FCSTD DOCUMENT  (FreeCAD 0.14R3702 (Git))
Label: big-gear-43_tooth-modified
License: CC-BY 3.0
LicenseURL: http://creativecommons.org/licenses/by/3.0/
objects: Part::Feature×1, Sketcher::SketchObject×1
note: 2 computed .brp shape members not serialized (recipe doc carries the construction recipe); baked Part::Feature solids carry a one-line shape summary decoded from their .brp

FEATURE [Part::Feature] Big_Gear_43_tooth_Less_Material001_solid  label="Big_Gear_43_tooth_Less_Material001 (Solid)"
  shape: large baked B-rep (63 MB .brp); summary skipped
FEATURE [Sketcher::SketchObject] Sketch
  ExternalGeometry = -> [Big_Gear_43_tooth_Less_Material001_solid]
  Placement = pos=(0,0,4) rot=(1,0,0;3.14159rad)
  Support = -> Big_Gear_43_tooth_Less_Material001_solid [Face22004]
  sketch-geometry (1):
    g0: LineSegment StartX=36.4279 StartY=-27.5004 StartZ=0 EndX=34.3053 EndY=-41.4336 EndZ=0
  constraints (4):
    c: PointOnObject(g0,g-4)
    c: Coincident(g0,g-5)
    c: Perpendicular(g0,g-4)
    c: Distance(g0) = 14.094
